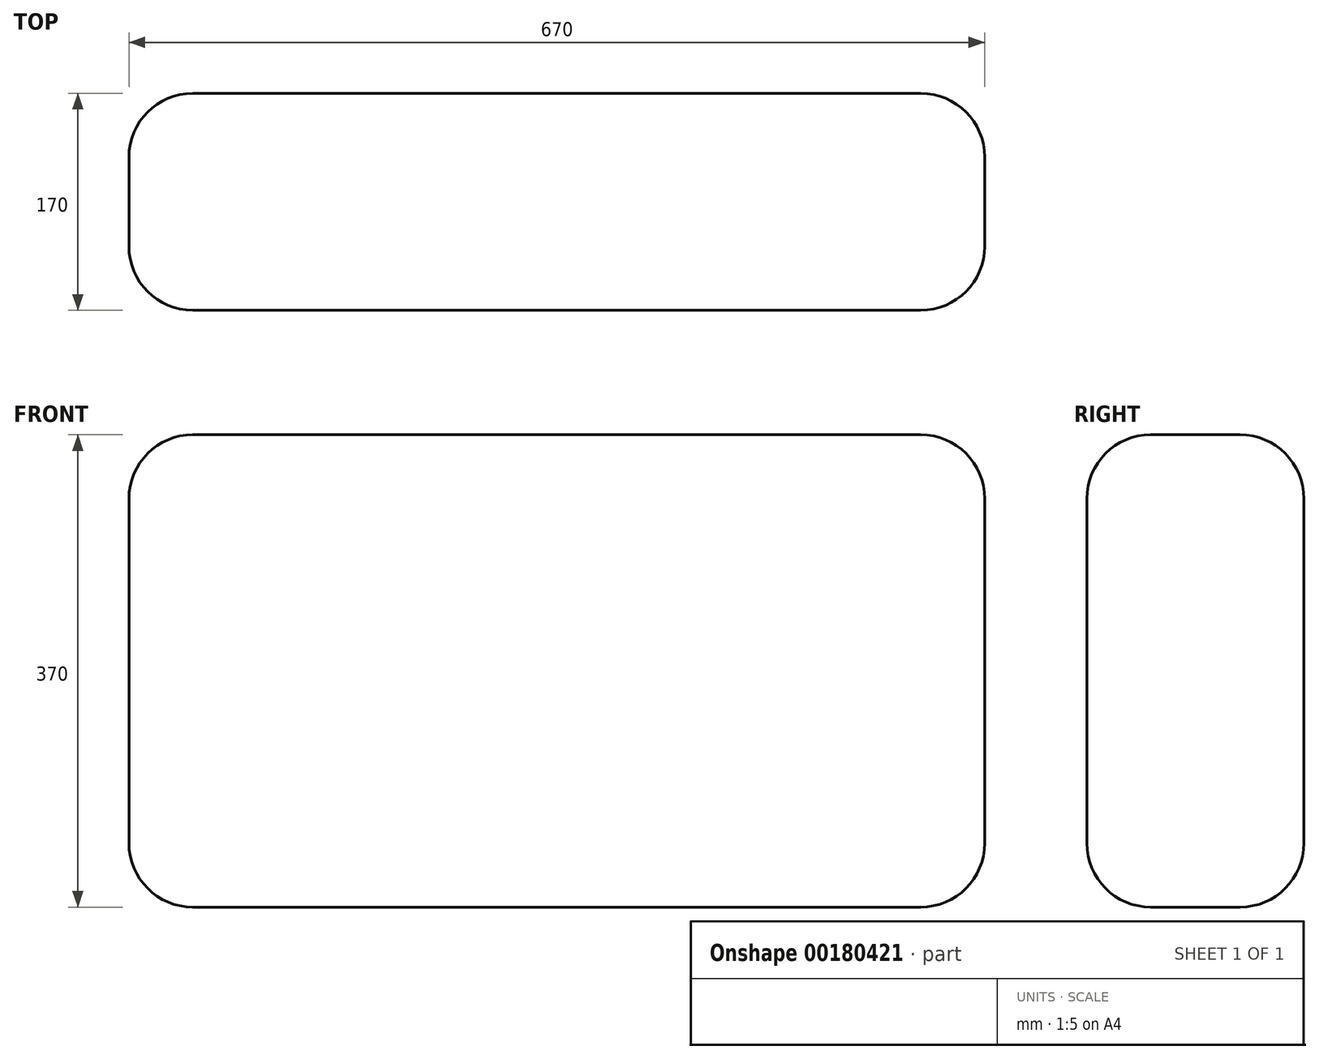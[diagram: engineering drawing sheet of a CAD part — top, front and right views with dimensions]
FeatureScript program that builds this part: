
annotation { "Feature Type Name" : "Feature", "Feature Type Description" : "" }
export const myFeature = defineFeature(function(context is Context, id is Id, definition is map)
    precondition{}
    {
        {
            var Q0;
            Q0=qCreatedBy(makeId("Top.planeOp"),FACE);
            var sketch = newSketch(context, id + "F0", { "sketchPlane" : qUnion([Q0])});
            skLineSegment(sketch, "E0.bottom", {"start": v(-336.66, 84.92) * mm, "end": v(333.34, 84.92) * mm});
            skLineSegment(sketch, "E0.top", {"start": v(-336.66, -85.08) * mm, "end": v(333.34, -85.08) * mm});
            skLineSegment(sketch, "E0.left", {"start": v(-336.66, 84.92) * mm, "end": v(-336.66, -85.08) * mm});
            skLineSegment(sketch, "E0.right", {"start": v(333.34, 84.92) * mm, "end": v(333.34, -85.08) * mm});
            skSolve(sketch);
        }
        {
            var Q0;
            Q0 = qSketchRegion(id + "F0", true);
            extrude(context, id + "F1", {"entities" : qUnion([Q0]), "depth" : 370 * mm});
        }
        {
            var Q0;
            Q0=makeQuery(id+"F1.opExtrude","CAP_EDGE",EDGE,{"disambiguationData":[OSD([sQuery(id+"F0.wireOp",EDGE,"E0.top")])],"isStart":false});
            var Q1;
            Q1=makeQuery(id+"F1.opExtrude","CAP_EDGE",EDGE,{"disambiguationData":[OSD([sQuery(id+"F0.wireOp",EDGE,"E0.top")])],"isStart":true});
            var Q2;
            Q2=makeQuery(id+"F1.opExtrude","SWEPT_EDGE",EDGE,{"disambiguationData":[OSD([sQuery(id+"F0.wireOp",EDGE,"E0.top"),sQuery(id+"F0.wireOp",EDGE,"E0.right")])]});
            var Q3;
            Q3=makeQuery(id+"F1.opExtrude","SWEPT_EDGE",EDGE,{"disambiguationData":[OSD([sQuery(id+"F0.wireOp",EDGE,"E0.bottom"),sQuery(id+"F0.wireOp",EDGE,"E0.right")])]});
            var Q4;
            Q4=makeQuery(id+"F1.opExtrude","CAP_EDGE",EDGE,{"disambiguationData":[OSD([sQuery(id+"F0.wireOp",EDGE,"E0.right")])],"isStart":false});
            var Q5;
            Q5=makeQuery(id+"F1.opExtrude","CAP_EDGE",EDGE,{"disambiguationData":[OSD([sQuery(id+"F0.wireOp",EDGE,"E0.right")])],"isStart":true});
            var Q6;
            Q6=makeQuery(id+"F1.opExtrude","CAP_EDGE",EDGE,{"disambiguationData":[OSD([sQuery(id+"F0.wireOp",EDGE,"E0.bottom")])],"isStart":false});
            var Q7;
            Q7=makeQuery(id+"F1.opExtrude","CAP_EDGE",EDGE,{"disambiguationData":[OSD([sQuery(id+"F0.wireOp",EDGE,"E0.bottom")])],"isStart":true});
            var Q8;
            Q8=makeQuery(id+"F1.opExtrude","SWEPT_EDGE",EDGE,{"disambiguationData":[OSD([sQuery(id+"F0.wireOp",EDGE,"E0.bottom"),sQuery(id+"F0.wireOp",EDGE,"E0.left")])]});
            var Q9;
            Q9=makeQuery(id+"F1.opExtrude","SWEPT_EDGE",EDGE,{"disambiguationData":[OSD([sQuery(id+"F0.wireOp",EDGE,"E0.top"),sQuery(id+"F0.wireOp",EDGE,"E0.left")])]});
            var Q10;
            Q10=makeQuery(id+"F1.opExtrude","CAP_EDGE",EDGE,{"disambiguationData":[OSD([sQuery(id+"F0.wireOp",EDGE,"E0.left")])],"isStart":false});
            var Q11;
            Q11=makeQuery(id+"F1.opExtrude","CAP_EDGE",EDGE,{"disambiguationData":[OSD([sQuery(id+"F0.wireOp",EDGE,"E0.left")])],"isStart":true});
            fillet(context, id + "F2", {"entities" : qUnion([Q0, Q1, Q2, Q3, Q4, Q5, Q6, Q7, Q8, Q9, Q10, Q11]), "radius" : 50 * mm, "tangentPropagation" : true, "allowEdgeOverflow" : false});
        }
    });
